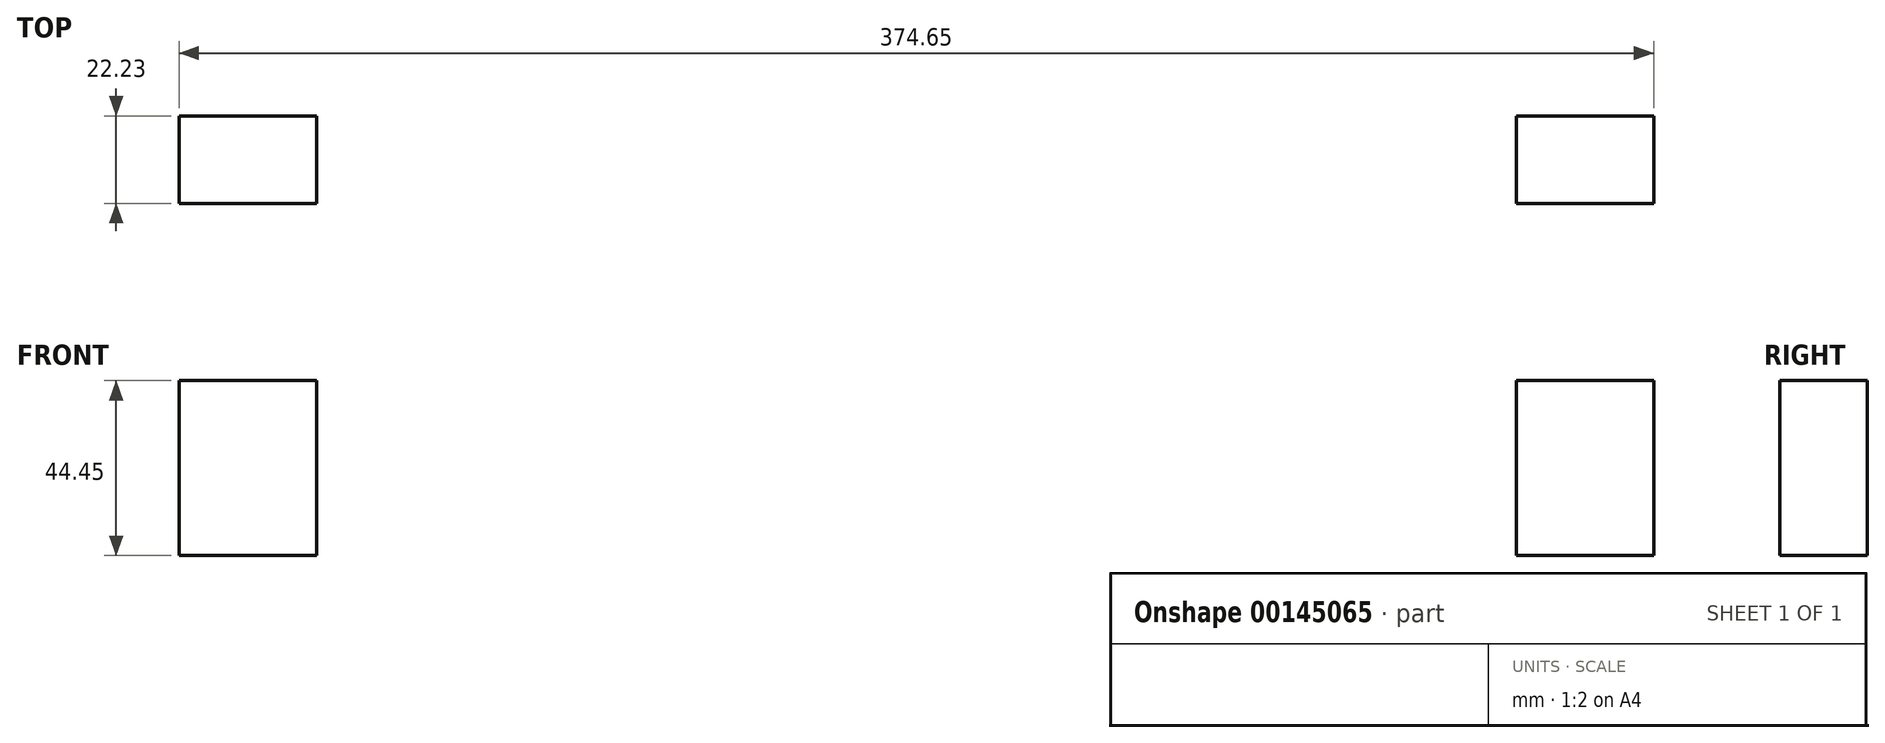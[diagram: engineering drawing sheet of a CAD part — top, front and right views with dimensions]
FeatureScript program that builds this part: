
annotation { "Feature Type Name" : "Feature", "Feature Type Description" : "" }
export const myFeature = defineFeature(function(context is Context, id is Id, definition is map)
    precondition{}
    {
        {
            var Q0;
            Q0=qCreatedBy(makeId("Front.planeOp"),FACE);
            var sketch = newSketch(context, id + "F0", { "sketchPlane" : qUnion([Q0])});
            skLineSegment(sketch, "E0.bottom", {"start": v(0, 0) * mm, "end": v(374.65, 0) * mm});
            skLineSegment(sketch, "E0.top", {"start": v(0, 101.6) * mm, "end": v(374.65, 101.6) * mm});
            skLineSegment(sketch, "E0.left", {"start": v(0, 0) * mm, "end": v(0, 101.6) * mm});
            skLineSegment(sketch, "E0.right", {"start": v(374.65, 0) * mm, "end": v(374.65, 101.6) * mm});
            skLineSegment(sketch, "E1.bottom", {"start": v(117.48, 0) * mm, "end": v(257.18, 0) * mm});
            skLineSegment(sketch, "E1.top", {"start": v(117.48, 19.05) * mm, "end": v(257.18, 19.05) * mm});
            skLineSegment(sketch, "E1.left", {"start": v(117.48, 0) * mm, "end": v(117.48, 19.05) * mm});
            skLineSegment(sketch, "E1.right", {"start": v(257.18, 0) * mm, "end": v(257.18, 19.05) * mm});
            skPoint(sketch, "E2.oppositeSnap0", {"position": v(0, 57.15) * mm});
            skLineSegment(sketch, "E2.bottom", {"start": v(0, 101.6) * mm, "end": v(34.92, 101.6) * mm});
            skLineSegment(sketch, "E2.top", {"start": v(0, 57.15) * mm, "end": v(34.92, 57.15) * mm});
            skLineSegment(sketch, "E2.left", {"start": v(0, 101.6) * mm, "end": v(0, 57.15) * mm});
            skLineSegment(sketch, "E2.right", {"start": v(34.92, 101.6) * mm, "end": v(34.92, 57.15) * mm});
            skLineSegment(sketch, "E3.bottom", {"start": v(339.73, 57.15) * mm, "end": v(374.65, 57.15) * mm});
            skLineSegment(sketch, "E3.top", {"start": v(339.73, 101.6) * mm, "end": v(374.65, 101.6) * mm});
            skLineSegment(sketch, "E3.left", {"start": v(339.73, 57.15) * mm, "end": v(339.73, 101.6) * mm});
            skLineSegment(sketch, "E3.right", {"start": v(374.65, 57.15) * mm, "end": v(374.65, 101.6) * mm});
            skSolve(sketch);
        }
        {
            var Q0;
            Q0=makeQuery(id+"F0.imprint","IMPRINT",FACE,{"disambiguationData":[TD([[makeQuery(id+"F0.imprint","IMPRINT",EDGE,{"derivedFrom":sQuery(id+"F0.wireOp",EDGE,"E0.top")}),-1.0]])]});
            extrude(context, id + "F1", {"entities" : qUnion([Q0]), "depth" : 22.22 * mm, "offsetDistance" : 25.4 * mm});
        }
        {
            var Q0;
            Q0=qCreatedBy(makeId("Top.planeOp"),FACE);
            var sketch = newSketch(context, id + "F2", { "sketchPlane" : qUnion([Q0])});
            skLineSegment(sketch, "E4.bottom", {"start": v(0, -15.88) * mm, "end": v(374.65, -15.88) * mm});
            skLineSegment(sketch, "E4.top", {"start": v(0, -6.35) * mm, "end": v(374.65, -6.35) * mm});
            skLineSegment(sketch, "E4.left", {"start": v(0, -15.88) * mm, "end": v(0, -6.35) * mm});
            skLineSegment(sketch, "E4.right", {"start": v(374.65, -15.88) * mm, "end": v(374.65, -6.35) * mm});
            skLineSegment(sketch, "E5.bottom", {"start": v(339.73, 0) * mm, "end": v(374.65, 0) * mm});
            skLineSegment(sketch, "E5.top", {"start": v(339.73, -22.23) * mm, "end": v(374.65, -22.23) * mm});
            skLineSegment(sketch, "E5.left", {"start": v(339.73, 0) * mm, "end": v(339.73, -22.23) * mm});
            skLineSegment(sketch, "E5.right", {"start": v(374.65, 0) * mm, "end": v(374.65, -22.23) * mm});
            skLineSegment(sketch, "E6.bottom", {"start": v(0, 0) * mm, "end": v(34.93, 0) * mm});
            skLineSegment(sketch, "E6.top", {"start": v(0, -22.23) * mm, "end": v(34.93, -22.23) * mm});
            skLineSegment(sketch, "E6.left", {"start": v(0, 0) * mm, "end": v(0, -22.23) * mm});
            skLineSegment(sketch, "E6.right", {"start": v(34.93, 0) * mm, "end": v(34.93, -22.23) * mm});
            skLineSegment(sketch, "E7", {"start": v(107.95, -15.88) * mm, "end": v(107.95, -6.35) * mm});
            skLineSegment(sketch, "E8", {"start": v(266.7, -15.88) * mm, "end": v(266.7, -6.35) * mm});
            skSolve(sketch);
        }
        {
            var Q0;
            {var subQ5=sQuery(id+"F2.wireOp",EDGE,"E5.top");Q0=makeQuery(id+"F2.imprint","IMPRINT",FACE,{"disambiguationData":[TD([[makeQuery(id+"F2.imprint","IMPRINT",EDGE,{"derivedFrom":subQ5}),1.0]])]});}
            var Q1;
            {var subQ5=sQuery(id+"F2.wireOp",EDGE,"E5.bottom");Q1=makeQuery(id+"F2.imprint","IMPRINT",FACE,{"disambiguationData":[TD([[makeQuery(id+"F2.imprint","IMPRINT",EDGE,{"derivedFrom":subQ5}),-1.0]])]});}
            var Q2;
            {var subQ5=sQuery(id+"F2.wireOp",EDGE,"E6.top");Q2=makeQuery(id+"F2.imprint","IMPRINT",FACE,{"disambiguationData":[TD([[makeQuery(id+"F2.imprint","IMPRINT",EDGE,{"derivedFrom":subQ5}),1.0]])]});}
            var Q3;
            {var subQ5=sQuery(id+"F2.wireOp",EDGE,"E6.bottom");Q3=makeQuery(id+"F2.imprint","IMPRINT",FACE,{"disambiguationData":[TD([[makeQuery(id+"F2.imprint","IMPRINT",EDGE,{"derivedFrom":subQ5}),-1.0]])]});}
            extrude(context, id + "F3", {"entities" : qUnion([Q0, Q1, Q2, Q3]), "operationType" : NewBodyOperationType.REMOVE, "endBound" : BoundingType.UP_TO_NEXT, "depth" : 25.4 * mm});
        }
        {
            var Q0;
            {var subQ0=sQuery(id+"F2.wireOp",EDGE,"E6.left");var subQ1=sQuery(id+"F2.wireOp",EDGE,"E4.bottom");var subQ2=makeQuery(id+"F2.imprint","INTERSECT",VERTEX,{"derivedFrom":[subQ1,subQ0]});Q0=makeQuery(id+"F2.imprint","IMPRINT",FACE,{"disambiguationData":[TD([[makeQuery(id+"F2.imprint","IMPRINT",EDGE,{"disambiguationData":[TD([[subQ2,-1.0]])],"derivedFrom":subQ1}),1.0]])]});}
            var Q1;
            {var subQ0=sQuery(id+"F2.wireOp",EDGE,"E6.right");var subQ1=sQuery(id+"F2.wireOp",EDGE,"E4.bottom");var subQ2=makeQuery(id+"F2.imprint","INTERSECT",VERTEX,{"derivedFrom":[subQ1,subQ0]});Q1=makeQuery(id+"F2.imprint","IMPRINT",FACE,{"disambiguationData":[TD([[makeQuery(id+"F2.imprint","IMPRINT",EDGE,{"disambiguationData":[TD([[subQ2,-1.0]])],"derivedFrom":subQ1}),1.0]])]});}
            var Q2;
            {var subQ0=sQuery(id+"F2.wireOp",EDGE,"E5.right");var subQ1=sQuery(id+"F2.wireOp",EDGE,"E4.bottom");var subQ2=makeQuery(id+"F2.imprint","INTERSECT",VERTEX,{"derivedFrom":[subQ1,subQ0]});Q2=makeQuery(id+"F2.imprint","IMPRINT",FACE,{"disambiguationData":[TD([[makeQuery(id+"F2.imprint","IMPRINT",EDGE,{"disambiguationData":[TD([[subQ2,1.0]])],"derivedFrom":subQ1}),1.0]])]});}
            var Q3;
            {var subQ0=sQuery(id+"F2.wireOp",EDGE,"E8");Q3=makeQuery(id+"F2.imprint","IMPRINT",FACE,{"disambiguationData":[TD([[makeQuery(id+"F2.imprint","IMPRINT",EDGE,{"derivedFrom":subQ0}),-1.0]])]});}
            var Q4;
            {var subQ0=sQuery(id+"F2.wireOp",EDGE,"E7");Q4=makeQuery(id+"F2.imprint","IMPRINT",FACE,{"disambiguationData":[TD([[makeQuery(id+"F2.imprint","IMPRINT",EDGE,{"derivedFrom":subQ0}),-1.0]])]});}
            extrude(context, id + "F4", {"entities" : qUnion([Q0, Q1, Q2, Q3, Q4]), "operationType" : NewBodyOperationType.REMOVE, "depth" : 9.52 * mm});
        }
        {
            var Q0;
            {var subQ0=sQuery(id+"F2.wireOp",EDGE,"E7");Q0=makeQuery(id+"F2.imprint","IMPRINT",FACE,{"disambiguationData":[TD([[makeQuery(id+"F2.imprint","IMPRINT",EDGE,{"derivedFrom":subQ0}),-1.0]])]});}
            extrude(context, id + "F5", {"entities" : qUnion([Q0]), "operationType" : NewBodyOperationType.REMOVE, "depth" : 28.57 * mm});
        }
    });
